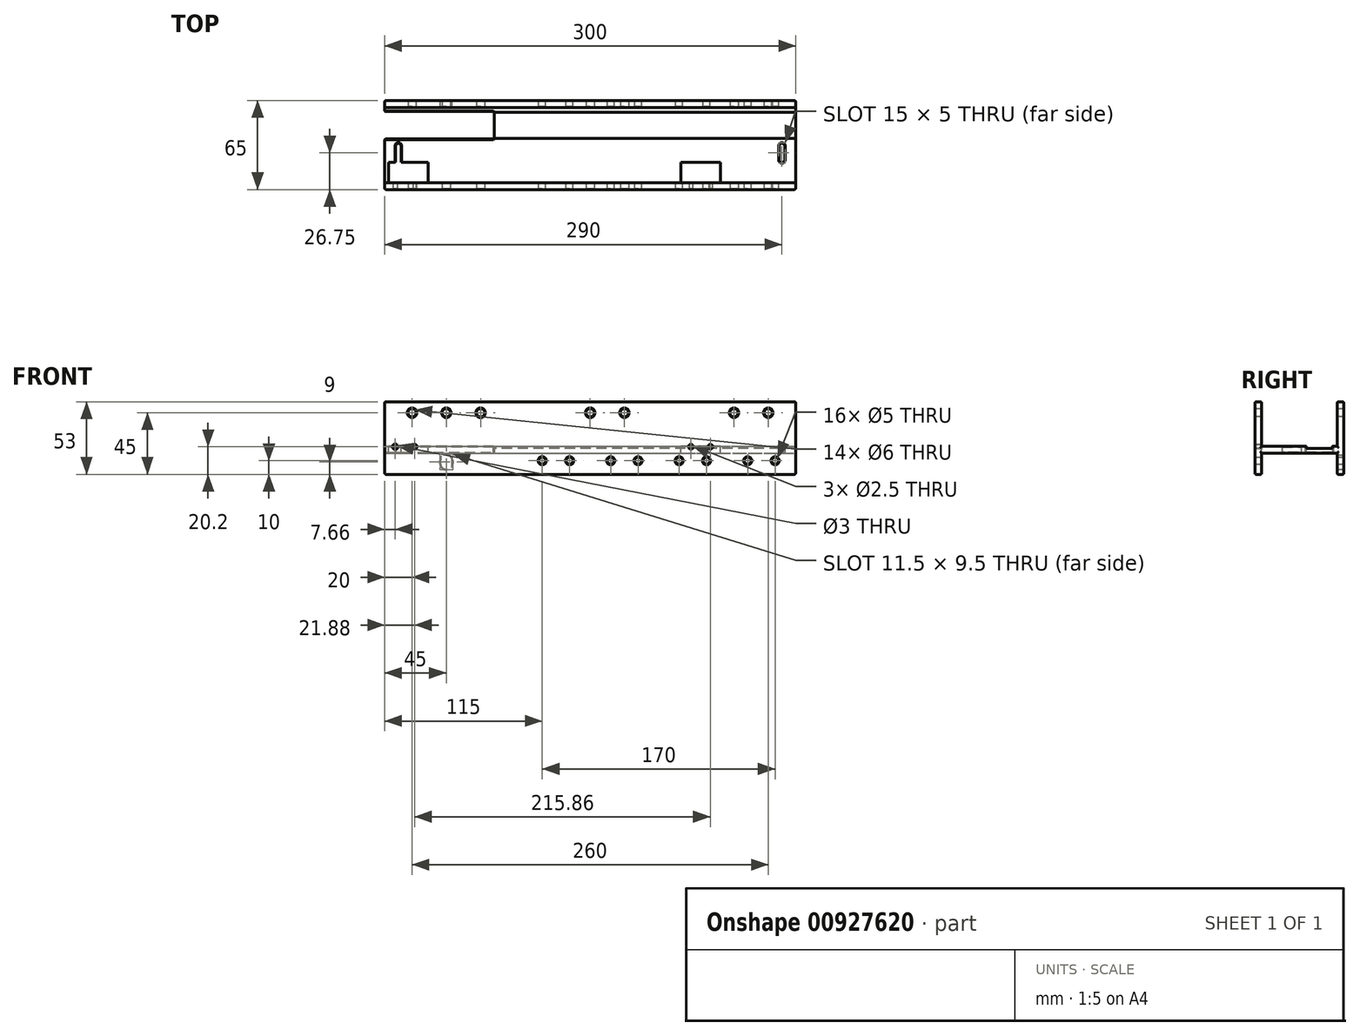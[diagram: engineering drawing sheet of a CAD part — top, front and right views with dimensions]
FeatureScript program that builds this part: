
annotation { "Feature Type Name" : "Feature", "Feature Type Description" : "" }
export const myFeature = defineFeature(function(context is Context, id is Id, definition is map)
    precondition{}
    {
        {
            var Q0;
            Q0=qCreatedBy(makeId("Right.planeOp"),FACE);
            var sketch = newSketch(context, id + "F0", { "sketchPlane" : qUnion([Q0])});
            skLineSegment(sketch, "E0", {"start": v(32.5, 30.09) * mm, "end": v(32.5, -3.64) * mm, "construction": true});
            skLineSegment(sketch, "E1", {"start": v(32.5, 20.5) * mm, "end": v(5, 20.5) * mm});
            skLineSegment(sketch, "E2", {"start": v(5, 20.5) * mm, "end": v(5, 53) * mm});
            skLineSegment(sketch, "E3", {"start": v(5, 53) * mm, "end": v(0, 53) * mm});
            skLineSegment(sketch, "E4", {"start": v(0, 53) * mm, "end": v(0, 0) * mm});
            skLineSegment(sketch, "E5", {"start": v(0, 0) * mm, "end": v(5, 0) * mm});
            skLineSegment(sketch, "E6", {"start": v(5, 0) * mm, "end": v(5, 15.5) * mm});
            skLineSegment(sketch, "E7", {"start": v(5, 15.5) * mm, "end": v(32.5, 15.5) * mm});
            skLineSegment(sketch, "E8.MirrorCS", {"start": v(32.5, 20.5) * mm, "end": v(60, 20.5) * mm});
            skLineSegment(sketch, "E9.MirrorCS", {"start": v(60, 15.5) * mm, "end": v(32.5, 15.5) * mm});
            skLineSegment(sketch, "E10.MirrorCS", {"start": v(60, 20.5) * mm, "end": v(60, 53) * mm});
            skLineSegment(sketch, "E11.MirrorCS", {"start": v(60, 53) * mm, "end": v(65, 53) * mm});
            skLineSegment(sketch, "E12.MirrorCS", {"start": v(65, 53) * mm, "end": v(65, 0) * mm});
            skLineSegment(sketch, "E13.MirrorCS", {"start": v(65, 0) * mm, "end": v(60, 0) * mm});
            skLineSegment(sketch, "E14.MirrorCS", {"start": v(60, 0) * mm, "end": v(60, 15.5) * mm});
            skLineSegment(sketch, "E15", {"start": v(26.34, 45) * mm, "end": v(97.95, 45) * mm, "construction": true});
            skLineSegment(sketch, "E16", {"start": v(29.5, 35.5) * mm, "end": v(100.2, 35.5) * mm, "construction": true});
            skLineSegment(sketch, "E17", {"start": v(30.7, 31) * mm, "end": v(101, 31) * mm, "construction": true});
            skSolve(sketch);
        }
        {
            var Q0;
            Q0=makeQuery(id+"F0.imprint","IMPRINT",FACE,{"disambiguationData":[TD([[makeQuery(id+"F0.imprint","IMPRINT",EDGE,{"derivedFrom":sQuery(id+"F0.wireOp",EDGE,"E1")}),1.0]])]});
            extrude(context, id + "F1", {"entities" : qUnion([Q0]), "oppositeDirection" : true, "depth" : 300 * mm, "offsetDistance" : 25 * mm});
        }
        {
            var Q0;
            Q0=makeQuery(id+"F1.opExtrude","SWEPT_FACE",FACE,{"disambiguationData":[OSD([sQuery(id+"F0.wireOp",EDGE,"E1"),sQuery(id+"F0.wireOp",EDGE,"E8.MirrorCS")])]});
            var sketch = newSketch(context, id + "F2", { "sketchPlane" : qUnion([Q0])});
            skLineSegment(sketch, "E18", {"start": v(-313.86, 45) * mm, "end": v(29.43, 45) * mm, "construction": true});
            skLineSegment(sketch, "E19", {"start": v(-150, 123.79) * mm, "end": v(-150, -54.38) * mm, "construction": true});
            skPoint(sketch, "E19.startSnap0", {"position": v(-150, 5) * mm});
            skLineSegment(sketch, "E20.MirrorCS", {"start": v(-220, 57) * mm, "end": v(-220, 45) * mm});
            skLineSegment(sketch, "E21.MirrorCS", {"start": v(-220, 37) * mm, "end": v(-220, 45) * mm});
            skLineSegment(sketch, "E22.MirrorCS", {"start": v(-300, 57) * mm, "end": v(-220, 57) * mm});
            skLineSegment(sketch, "E23.MirrorCS", {"start": v(-300, 37) * mm, "end": v(-220, 37) * mm});
            skSolve(sketch);
        }
        {
            var Q0;
            Q0=makeQuery(id+"F2.imprint","IMPRINT",FACE,{"disambiguationData":[TD([[makeQuery(id+"F2.imprint","IMPRINT",EDGE,{"derivedFrom":sQuery(id+"F2.wireOp",EDGE,"E20.MirrorCS")}),-1.0]])]});
            var Q1;
            {var subQ1=sQuery(id+"F2.wireOp",EDGE,"GCHkkF9p-yWQI-8tYB-lPff-ol5Ikm6K2We2");Q1=makeQuery(id+"F2.imprint","IMPRINT",FACE,{"disambiguationData":[TD([[makeQuery(id+"F2.imprint","IMPRINT",EDGE,{"derivedFrom":subQ1}),1.0]])]});}
            extrude(context, id + "F3", {"entities" : qUnion([Q0, Q1]), "operationType" : NewBodyOperationType.REMOVE, "endBound" : BoundingType.THROUGH_ALL, "oppositeDirection" : true, "depth" : 25 * mm, "offsetDistance" : 25 * mm});
        }
        {
            var Q0;
            Q0=makeQuery(id+"F1.opExtrude","SWEPT_EDGE",EDGE,{"disambiguationData":[OSD([sQuery(id+"F0.wireOp",EDGE,"E11.MirrorCS"),sQuery(id+"F0.wireOp",EDGE,"E12.MirrorCS")])]});
            var Q1;
            Q1=makeQuery(id+"F1.opExtrude","SWEPT_EDGE",EDGE,{"disambiguationData":[OSD([sQuery(id+"F0.wireOp",EDGE,"E3"),sQuery(id+"F0.wireOp",EDGE,"E4")])]});
            var Q2;
            Q2=makeQuery(id+"F1.opExtrude","SWEPT_EDGE",EDGE,{"disambiguationData":[OSD([sQuery(id+"F0.wireOp",EDGE,"E4"),sQuery(id+"F0.wireOp",EDGE,"E5")])]});
            var Q3;
            Q3=makeQuery(id+"F1.opExtrude","SWEPT_EDGE",EDGE,{"disambiguationData":[OSD([sQuery(id+"F0.wireOp",EDGE,"E5"),sQuery(id+"F0.wireOp",EDGE,"E6")])]});
            var Q4;
            Q4=makeQuery(id+"F1.opExtrude","SWEPT_EDGE",EDGE,{"disambiguationData":[OSD([sQuery(id+"F0.wireOp",EDGE,"E13.MirrorCS"),sQuery(id+"F0.wireOp",EDGE,"E14.MirrorCS")])]});
            var Q5;
            Q5=makeQuery(id+"F1.opExtrude","SWEPT_EDGE",EDGE,{"disambiguationData":[OSD([sQuery(id+"F0.wireOp",EDGE,"E12.MirrorCS"),sQuery(id+"F0.wireOp",EDGE,"E13.MirrorCS")])]});
            var Q6;
            Q6=makeQuery(id+"F1.opExtrude","SWEPT_EDGE",EDGE,{"disambiguationData":[OSD([sQuery(id+"F0.wireOp",EDGE,"E2"),sQuery(id+"F0.wireOp",EDGE,"E3")])]});
            var Q7;
            Q7=makeQuery(id+"F1.opExtrude","SWEPT_EDGE",EDGE,{"disambiguationData":[OSD([sQuery(id+"F0.wireOp",EDGE,"E10.MirrorCS"),sQuery(id+"F0.wireOp",EDGE,"E11.MirrorCS")])]});
            var Q8;
            Q8=makeQuery(id+"F1.opExtrude","CAP_EDGE",EDGE,{"disambiguationData":[OSD([sQuery(id+"F0.wireOp",EDGE,"E4")])],"isStart":true});
            var Q9;
            Q9=makeQuery(id+"F1.opExtrude","CAP_EDGE",EDGE,{"disambiguationData":[OSD([sQuery(id+"F0.wireOp",EDGE,"E2")])],"isStart":true});
            var Q10;
            {var subQ0=sQuery(id+"F0.wireOp",EDGE,"E8.MirrorCS");var subQ1=sQuery(id+"F0.wireOp",EDGE,"E2");var subQ2=sQuery(id+"F0.wireOp",EDGE,"E1");Q10=makeQuery(id+"F3.boolean.opBoolean","SPLIT",EDGE,{"disambiguationData":[TD([makeQuery(id+"F1.opExtrude","SWEPT_FACE",FACE,{"disambiguationData":[OSD([subQ1])]})])],"derivedFrom":makeQuery(id+"F1.opExtrude","CAP_EDGE",EDGE,{"disambiguationData":[OSD([subQ2,subQ0])],"isStart":true})});}
            var Q11;
            Q11=makeQuery(id+"F1.opExtrude","CAP_EDGE",EDGE,{"disambiguationData":[OSD([sQuery(id+"F0.wireOp",EDGE,"E6")])],"isStart":true});
            var Q12;
            Q12=makeQuery(id+"F1.opExtrude","CAP_EDGE",EDGE,{"disambiguationData":[OSD([sQuery(id+"F0.wireOp",EDGE,"E3")])],"isStart":true});
            var Q13;
            Q13=makeQuery(id+"F1.opExtrude","CAP_EDGE",EDGE,{"disambiguationData":[OSD([sQuery(id+"F0.wireOp",EDGE,"E5")])],"isStart":true});
            var Q14;
            Q14=makeQuery(id+"F1.opExtrude","CAP_EDGE",EDGE,{"disambiguationData":[OSD([sQuery(id+"F0.wireOp",EDGE,"E13.MirrorCS")])],"isStart":true});
            var Q15;
            Q15=makeQuery(id+"F1.opExtrude","CAP_EDGE",EDGE,{"disambiguationData":[OSD([sQuery(id+"F0.wireOp",EDGE,"E11.MirrorCS")])],"isStart":true});
            var Q16;
            Q16=makeQuery(id+"F1.opExtrude","CAP_EDGE",EDGE,{"disambiguationData":[OSD([sQuery(id+"F0.wireOp",EDGE,"E12.MirrorCS")])],"isStart":true});
            var Q17;
            Q17=makeQuery(id+"F1.opExtrude","CAP_EDGE",EDGE,{"disambiguationData":[OSD([sQuery(id+"F0.wireOp",EDGE,"E10.MirrorCS")])],"isStart":true});
            var Q18;
            Q18=makeQuery(id+"F1.opExtrude","CAP_EDGE",EDGE,{"disambiguationData":[OSD([sQuery(id+"F0.wireOp",EDGE,"E14.MirrorCS")])],"isStart":true});
            var Q19;
            {var subQ0=sQuery(id+"F0.wireOp",EDGE,"E10.MirrorCS");var subQ1=sQuery(id+"F0.wireOp",EDGE,"E8.MirrorCS");var subQ2=sQuery(id+"F0.wireOp",EDGE,"E1");Q19=makeQuery(id+"F3.boolean.opBoolean","SPLIT",EDGE,{"disambiguationData":[TD([makeQuery(id+"F1.opExtrude","SWEPT_FACE",FACE,{"disambiguationData":[OSD([subQ0])]})])],"derivedFrom":makeQuery(id+"F1.opExtrude","CAP_EDGE",EDGE,{"disambiguationData":[OSD([subQ2,subQ1])],"isStart":true})});}
            var Q20;
            {var subQ0=sQuery(id+"F0.wireOp",EDGE,"E9.MirrorCS");var subQ1=sQuery(id+"F0.wireOp",EDGE,"E7");var subQ2=sQuery(id+"F0.wireOp",EDGE,"E6");Q20=makeQuery(id+"F3.boolean.opBoolean","SPLIT",EDGE,{"disambiguationData":[TD([makeQuery(id+"F1.opExtrude","SWEPT_FACE",FACE,{"disambiguationData":[OSD([subQ2])]})])],"derivedFrom":makeQuery(id+"F1.opExtrude","CAP_EDGE",EDGE,{"disambiguationData":[OSD([subQ1,subQ0])],"isStart":true})});}
            var Q21;
            Q21=makeQuery(id+"F1.opExtrude","CAP_EDGE",EDGE,{"disambiguationData":[OSD([sQuery(id+"F0.wireOp",EDGE,"E5")])],"isStart":false});
            var Q22;
            Q22=makeQuery(id+"F1.opExtrude","CAP_EDGE",EDGE,{"disambiguationData":[OSD([sQuery(id+"F0.wireOp",EDGE,"E4")])],"isStart":false});
            var Q23;
            Q23=makeQuery(id+"F1.opExtrude","CAP_EDGE",EDGE,{"disambiguationData":[OSD([sQuery(id+"F0.wireOp",EDGE,"E3")])],"isStart":false});
            var Q24;
            Q24=makeQuery(id+"F1.opExtrude","CAP_EDGE",EDGE,{"disambiguationData":[OSD([sQuery(id+"F0.wireOp",EDGE,"E2")])],"isStart":false});
            var Q25;
            Q25=makeQuery(id+"F1.opExtrude","CAP_EDGE",EDGE,{"disambiguationData":[OSD([sQuery(id+"F0.wireOp",EDGE,"E6")])],"isStart":false});
            var Q26;
            {var subQ0=sQuery(id+"F0.wireOp",EDGE,"E9.MirrorCS");var subQ1=sQuery(id+"F0.wireOp",EDGE,"E7");var subQ2=sQuery(id+"F0.wireOp",EDGE,"E6");Q26=makeQuery(id+"F3.boolean.opBoolean","SPLIT",EDGE,{"disambiguationData":[TD([makeQuery(id+"F1.opExtrude","SWEPT_FACE",FACE,{"disambiguationData":[OSD([subQ2])]})])],"derivedFrom":makeQuery(id+"F1.opExtrude","CAP_EDGE",EDGE,{"disambiguationData":[OSD([subQ1,subQ0])],"isStart":false})});}
            var Q27;
            {var subQ0=sQuery(id+"F0.wireOp",EDGE,"E8.MirrorCS");var subQ1=sQuery(id+"F0.wireOp",EDGE,"E2");var subQ2=sQuery(id+"F0.wireOp",EDGE,"E1");Q27=makeQuery(id+"F3.boolean.opBoolean","SPLIT",EDGE,{"disambiguationData":[TD([makeQuery(id+"F1.opExtrude","SWEPT_FACE",FACE,{"disambiguationData":[OSD([subQ1])]})])],"derivedFrom":makeQuery(id+"F1.opExtrude","CAP_EDGE",EDGE,{"disambiguationData":[OSD([subQ2,subQ0])],"isStart":false})});}
            var Q28;
            Q28=makeQuery(id+"F1.opExtrude","CAP_EDGE",EDGE,{"disambiguationData":[OSD([sQuery(id+"F0.wireOp",EDGE,"E14.MirrorCS")])],"isStart":false});
            var Q29;
            Q29=makeQuery(id+"F1.opExtrude","CAP_EDGE",EDGE,{"disambiguationData":[OSD([sQuery(id+"F0.wireOp",EDGE,"E13.MirrorCS")])],"isStart":false});
            var Q30;
            Q30=makeQuery(id+"F1.opExtrude","CAP_EDGE",EDGE,{"disambiguationData":[OSD([sQuery(id+"F0.wireOp",EDGE,"E12.MirrorCS")])],"isStart":false});
            var Q31;
            Q31=makeQuery(id+"F1.opExtrude","CAP_EDGE",EDGE,{"disambiguationData":[OSD([sQuery(id+"F0.wireOp",EDGE,"E11.MirrorCS")])],"isStart":false});
            var Q32;
            Q32=makeQuery(id+"F1.opExtrude","CAP_EDGE",EDGE,{"disambiguationData":[OSD([sQuery(id+"F0.wireOp",EDGE,"E10.MirrorCS")])],"isStart":false});
            var Q33;
            {var subQ0=sQuery(id+"F0.wireOp",EDGE,"E10.MirrorCS");var subQ1=sQuery(id+"F0.wireOp",EDGE,"E8.MirrorCS");var subQ2=sQuery(id+"F0.wireOp",EDGE,"E1");Q33=makeQuery(id+"F3.boolean.opBoolean","SPLIT",EDGE,{"disambiguationData":[TD([makeQuery(id+"F1.opExtrude","SWEPT_FACE",FACE,{"disambiguationData":[OSD([subQ0])]})])],"derivedFrom":makeQuery(id+"F1.opExtrude","CAP_EDGE",EDGE,{"disambiguationData":[OSD([subQ2,subQ1])],"isStart":false})});}
            var Q34;
            {var subQ0=sQuery(id+"F0.wireOp",EDGE,"E14.MirrorCS");var subQ1=sQuery(id+"F0.wireOp",EDGE,"E9.MirrorCS");var subQ2=sQuery(id+"F0.wireOp",EDGE,"E7");Q34=makeQuery(id+"F3.boolean.opBoolean","SPLIT",EDGE,{"disambiguationData":[TD([makeQuery(id+"F1.opExtrude","SWEPT_FACE",FACE,{"disambiguationData":[OSD([subQ0])]})])],"derivedFrom":makeQuery(id+"F1.opExtrude","CAP_EDGE",EDGE,{"disambiguationData":[OSD([subQ2,subQ1])],"isStart":false})});}
            fillet(context, id + "F4", {"entities" : qUnion([Q0, Q1, Q2, Q3, Q4, Q5, Q6, Q7, Q8, Q9, Q10, Q11, Q12, Q13, Q14, Q15, Q16, Q17, Q18, Q19, Q20, Q21, Q22, Q23, Q24, Q25, Q26, Q27, Q28, Q29, Q30, Q31, Q32, Q33, Q34]), "radius" : 1 * mm, "tangentPropagation" : true, "allowEdgeOverflow" : false});
        }
        {
            var Q0;
            Q0=qCreatedBy(makeId("Front.planeOp"),FACE);
            var sketch = newSketch(context, id + "F5", { "sketchPlane" : qUnion([Q0])});
            skLineSegment(sketch, "E24.0.0", {"start": v(-299, 1) * mm, "end": v(-1, 1) * mm});
            skLineSegment(sketch, "E24.0.1", {"start": v(-1, 1) * mm, "end": v(-1, 52) * mm});
            skLineSegment(sketch, "E24.0.2", {"start": v(-1, 52) * mm, "end": v(-299, 52) * mm});
            skLineSegment(sketch, "E24.0.3", {"start": v(-299, 52) * mm, "end": v(-299, 1) * mm});
            skLineSegment(sketch, "E25", {"start": v(-345.84, 45) * mm, "end": v(41.43, 45) * mm, "construction": true});
            skCircle(sketch, "E26", {"center": v(-20, 45) * mm, "radius": 3 * mm});
            skCircle(sketch, "E27.1.0.0", {"center": v(-45, 45) * mm, "radius": 3 * mm});
            skLineSegment(sketch, "E27.direction1", {"start": v(-20, 45) * mm, "end": v(-45, 45) * mm, "construction": true});
            skCircle(sketch, "E28", {"center": v(-280, 45) * mm, "radius": 3 * mm});
            skCircle(sketch, "E29.1.0.0", {"center": v(-255, 45) * mm, "radius": 3 * mm});
            skCircle(sketch, "E29.2.0.0", {"center": v(-230, 45) * mm, "radius": 3 * mm});
            skLineSegment(sketch, "E29.direction1", {"start": v(-280, 45) * mm, "end": v(-255, 45) * mm, "construction": true});
            skLineSegment(sketch, "E30", {"start": v(-150, 104.95) * mm, "end": v(-150, -59.13) * mm, "construction": true});
            skCircle(sketch, "E31", {"center": v(-150, 45) * mm, "radius": 3 * mm});
            skCircle(sketch, "E32.1.0.0", {"center": v(-125, 45) * mm, "radius": 3 * mm});
            skLineSegment(sketch, "E32.direction1", {"start": v(-150, 45) * mm, "end": v(-125, 45) * mm, "construction": true});
            skLineSegment(sketch, "E33.direction1", {"start": v(-150, 45) * mm, "end": v(-175, 45) * mm, "construction": true});
            skCircle(sketch, "E34", {"center": v(-45, 45) * mm, "radius": 9.5 * mm, "construction": true});
            skLineSegment(sketch, "E35", {"start": v(-54.5, 62.62) * mm, "end": v(-54.5, 11.97) * mm, "construction": true});
            skLineSegment(sketch, "E36", {"start": v(-57.5, 61.94) * mm, "end": v(-57.5, 10.88) * mm, "construction": true});
            skLineSegment(sketch, "E37", {"start": v(-94.96, 20.2) * mm, "end": v(-48.41, 20.2) * mm, "construction": true});
            skLineSegment(sketch, "E38", {"start": v(-94.06, 14.9) * mm, "end": v(-44.37, 14.9) * mm, "construction": true});
            skCircle(sketch, "E39", {"center": v(-62.26, 20.2) * mm, "radius": 1.25 * mm});
            skCircle(sketch, "E40", {"center": v(-76.48, 20.2) * mm, "radius": 1.25 * mm});
            skCircle(sketch, "E41", {"center": v(-230, 45) * mm, "radius": 9.5 * mm, "construction": true});
            skLineSegment(sketch, "E42", {"start": v(-297.1, 57.68) * mm, "end": v(-297.1, 12.3) * mm, "construction": true});
            skLineSegment(sketch, "E43", {"start": v(-224.68, 20.2) * mm, "end": v(-186.08, 20.2) * mm, "construction": true});
            skCircle(sketch, "E44", {"center": v(-292.34, 20.2) * mm, "radius": 1.5 * mm});
            skCircle(sketch, "E45", {"center": v(-278.12, 20.2) * mm, "radius": 1.25 * mm});
            skLineSegment(sketch, "E46", {"start": v(-217.85, 25.5) * mm, "end": v(-182.53, 25.5) * mm, "construction": true});
            skLineSegment(sketch, "E47", {"start": v(-218.26, 14.9) * mm, "end": v(-182.12, 14.9) * mm, "construction": true});
            skLineSegment(sketch, "E48", {"start": v(-92.25, 25.5) * mm, "end": v(-56.75, 25.5) * mm, "construction": true});
            skLineSegment(sketch, "E49", {"start": v(-273.36, 59.39) * mm, "end": v(-273.36, 11.5) * mm, "construction": true});
            skLineSegment(sketch, "E50", {"start": v(-247.58, 30.5) * mm, "end": v(-217.06, 30.5) * mm, "construction": true});
            skLineSegment(sketch, "E51", {"start": v(-30.25, 30.5) * mm, "end": v(-63.73, 30.5) * mm, "construction": true});
            skLineSegment(sketch, "E52", {"start": v(-69.37, 53.38) * mm, "end": v(-69.37, 2.85) * mm, "construction": true});
            skLineSegment(sketch, "E53", {"start": v(-285.23, 36.68) * mm, "end": v(-285.23, 10.56) * mm, "construction": true});
            skLineSegment(sketch, "E54", {"start": v(-215.5, 60.74) * mm, "end": v(-215.5, -20.98) * mm, "construction": true});
            skSolve(sketch);
        }
        {
            var Q0;
            Q0=makeQuery(id+"F5.imprint","IMPRINT",FACE,{"disambiguationData":[TD([[makeQuery(id+"F5.imprint","IMPRINT",EDGE,{"derivedFrom":sQuery(id+"F5.wireOp",EDGE,"E26")}),1.0]])]});
            var Q1;
            Q1=makeQuery(id+"F5.imprint","IMPRINT",FACE,{"disambiguationData":[TD([[makeQuery(id+"F5.imprint","IMPRINT",EDGE,{"derivedFrom":sQuery(id+"F5.wireOp",EDGE,"E27.1.0.0")}),1.0]])]});
            var Q2;
            Q2=makeQuery(id+"F5.imprint","IMPRINT",FACE,{"disambiguationData":[TD([[makeQuery(id+"F5.imprint","IMPRINT",EDGE,{"derivedFrom":sQuery(id+"F5.wireOp",EDGE,"E27.2.0.0")}),1.0]])]});
            var Q3;
            Q3=makeQuery(id+"F5.imprint","IMPRINT",FACE,{"disambiguationData":[TD([[makeQuery(id+"F5.imprint","IMPRINT",EDGE,{"derivedFrom":sQuery(id+"F5.wireOp",EDGE,"E32.2.0.0")}),1.0]])]});
            var Q4;
            Q4=makeQuery(id+"F5.imprint","IMPRINT",FACE,{"disambiguationData":[TD([[makeQuery(id+"F5.imprint","IMPRINT",EDGE,{"derivedFrom":sQuery(id+"F5.wireOp",EDGE,"E32.1.0.0")}),1.0]])]});
            var Q5;
            Q5=makeQuery(id+"F5.imprint","IMPRINT",FACE,{"disambiguationData":[TD([[makeQuery(id+"F5.imprint","IMPRINT",EDGE,{"derivedFrom":sQuery(id+"F5.wireOp",EDGE,"E31")}),1.0]])]});
            var Q6;
            Q6=makeQuery(id+"F5.imprint","IMPRINT",FACE,{"disambiguationData":[TD([[makeQuery(id+"F5.imprint","IMPRINT",EDGE,{"derivedFrom":sQuery(id+"F5.wireOp",EDGE,"E33.1.0.0")}),1.0]])]});
            var Q7;
            Q7=makeQuery(id+"F5.imprint","IMPRINT",FACE,{"disambiguationData":[TD([[makeQuery(id+"F5.imprint","IMPRINT",EDGE,{"derivedFrom":sQuery(id+"F5.wireOp",EDGE,"E28")}),1.0]])]});
            var Q8;
            Q8=makeQuery(id+"F5.imprint","IMPRINT",FACE,{"disambiguationData":[TD([[makeQuery(id+"F5.imprint","IMPRINT",EDGE,{"derivedFrom":sQuery(id+"F5.wireOp",EDGE,"E29.1.0.0")}),1.0]])]});
            var Q9;
            Q9=makeQuery(id+"F5.imprint","IMPRINT",FACE,{"disambiguationData":[TD([[makeQuery(id+"F5.imprint","IMPRINT",EDGE,{"derivedFrom":sQuery(id+"F5.wireOp",EDGE,"E29.2.0.0")}),1.0]])]});
            var Q10;
            Q10=makeQuery(id+"F5.imprint","IMPRINT",FACE,{"disambiguationData":[TD([[makeQuery(id+"F5.imprint","IMPRINT",EDGE,{"derivedFrom":sQuery(id+"F5.wireOp",EDGE,"E33.2.0.0")}),1.0]])]});
            extrude(context, id + "F6", {"entities" : qUnion([Q0, Q1, Q2, Q3, Q4, Q5, Q6, Q7, Q8, Q9, Q10]), "operationType" : NewBodyOperationType.REMOVE, "endBound" : BoundingType.THROUGH_ALL, "oppositeDirection" : true, "depth" : 25 * mm, "offsetDistance" : 25 * mm});
        }
        {
            var Q0;
            Q0=makeQuery(id+"F6.boolean.opBoolean","COPY",FACE,{"disambiguationData":[TD([makeQuery(id+"F1.opExtrude","SWEPT_FACE",FACE,{"disambiguationData":[OSD([sQuery(id+"F0.wireOp",EDGE,"E2")])]})])],"derivedFrom":makeQuery(id+"F6.opExtrude","SWEPT_FACE",FACE,{"disambiguationData":[OSD([sQuery(id+"F5.wireOp",EDGE,"E26")])]})});
            var Q1;
            Q1=makeQuery(id+"F6.boolean.opBoolean","COPY",FACE,{"disambiguationData":[TD([makeQuery(id+"F1.opExtrude","SWEPT_FACE",FACE,{"disambiguationData":[OSD([sQuery(id+"F0.wireOp",EDGE,"E2")])]})])],"derivedFrom":makeQuery(id+"F6.opExtrude","SWEPT_FACE",FACE,{"disambiguationData":[OSD([sQuery(id+"F5.wireOp",EDGE,"E27.1.0.0")])]})});
            var Q2;
            Q2=makeQuery(id+"F6.boolean.opBoolean","COPY",FACE,{"disambiguationData":[TD([makeQuery(id+"F1.opExtrude","SWEPT_FACE",FACE,{"disambiguationData":[OSD([sQuery(id+"F0.wireOp",EDGE,"E2")])]})])],"derivedFrom":makeQuery(id+"F6.opExtrude","SWEPT_FACE",FACE,{"disambiguationData":[OSD([sQuery(id+"F5.wireOp",EDGE,"E27.2.0.0")])]})});
            var Q3;
            Q3=makeQuery(id+"F6.boolean.opBoolean","COPY",FACE,{"disambiguationData":[TD([makeQuery(id+"F1.opExtrude","SWEPT_FACE",FACE,{"disambiguationData":[OSD([sQuery(id+"F0.wireOp",EDGE,"E2")])]})])],"derivedFrom":makeQuery(id+"F6.opExtrude","SWEPT_FACE",FACE,{"disambiguationData":[OSD([sQuery(id+"F5.wireOp",EDGE,"E32.2.0.0")])]})});
            var Q4;
            Q4=makeQuery(id+"F6.boolean.opBoolean","COPY",FACE,{"disambiguationData":[TD([makeQuery(id+"F1.opExtrude","SWEPT_FACE",FACE,{"disambiguationData":[OSD([sQuery(id+"F0.wireOp",EDGE,"E2")])]})])],"derivedFrom":makeQuery(id+"F6.opExtrude","SWEPT_FACE",FACE,{"disambiguationData":[OSD([sQuery(id+"F5.wireOp",EDGE,"E32.1.0.0")])]})});
            var Q5;
            Q5=makeQuery(id+"F6.boolean.opBoolean","COPY",FACE,{"disambiguationData":[TD([makeQuery(id+"F1.opExtrude","SWEPT_FACE",FACE,{"disambiguationData":[OSD([sQuery(id+"F0.wireOp",EDGE,"E2")])]})])],"derivedFrom":makeQuery(id+"F6.opExtrude","SWEPT_FACE",FACE,{"disambiguationData":[OSD([sQuery(id+"F5.wireOp",EDGE,"E31")])]})});
            var Q6;
            Q6=makeQuery(id+"F6.boolean.opBoolean","COPY",FACE,{"disambiguationData":[TD([makeQuery(id+"F1.opExtrude","SWEPT_FACE",FACE,{"disambiguationData":[OSD([sQuery(id+"F0.wireOp",EDGE,"E2")])]})])],"derivedFrom":makeQuery(id+"F6.opExtrude","SWEPT_FACE",FACE,{"disambiguationData":[OSD([sQuery(id+"F5.wireOp",EDGE,"E33.1.0.0")])]})});
            var Q7;
            Q7=makeQuery(id+"F6.boolean.opBoolean","COPY",FACE,{"disambiguationData":[TD([makeQuery(id+"F1.opExtrude","SWEPT_FACE",FACE,{"disambiguationData":[OSD([sQuery(id+"F0.wireOp",EDGE,"E2")])]})])],"derivedFrom":makeQuery(id+"F6.opExtrude","SWEPT_FACE",FACE,{"disambiguationData":[OSD([sQuery(id+"F5.wireOp",EDGE,"E33.2.0.0")])]})});
            var Q8;
            Q8=makeQuery(id+"F6.boolean.opBoolean","COPY",FACE,{"disambiguationData":[TD([makeQuery(id+"F1.opExtrude","SWEPT_FACE",FACE,{"disambiguationData":[OSD([sQuery(id+"F0.wireOp",EDGE,"E2")])]})])],"derivedFrom":makeQuery(id+"F6.opExtrude","SWEPT_FACE",FACE,{"disambiguationData":[OSD([sQuery(id+"F5.wireOp",EDGE,"E29.2.0.0")])]})});
            var Q9;
            Q9=makeQuery(id+"F6.boolean.opBoolean","COPY",FACE,{"disambiguationData":[TD([makeQuery(id+"F1.opExtrude","SWEPT_FACE",FACE,{"disambiguationData":[OSD([sQuery(id+"F0.wireOp",EDGE,"E2")])]})])],"derivedFrom":makeQuery(id+"F6.opExtrude","SWEPT_FACE",FACE,{"disambiguationData":[OSD([sQuery(id+"F5.wireOp",EDGE,"E29.1.0.0")])]})});
            var Q10;
            Q10=makeQuery(id+"F6.boolean.opBoolean","COPY",FACE,{"disambiguationData":[TD([makeQuery(id+"F1.opExtrude","SWEPT_FACE",FACE,{"disambiguationData":[OSD([sQuery(id+"F0.wireOp",EDGE,"E2")])]})])],"derivedFrom":makeQuery(id+"F6.opExtrude","SWEPT_FACE",FACE,{"disambiguationData":[OSD([sQuery(id+"F5.wireOp",EDGE,"E28")])]})});
            var Q11;
            Q11=makeQuery(id+"F6.boolean.opBoolean","COPY",FACE,{"disambiguationData":[TD([makeQuery(id+"F1.opExtrude","SWEPT_FACE",FACE,{"disambiguationData":[OSD([sQuery(id+"F0.wireOp",EDGE,"E10.MirrorCS")])]})])],"derivedFrom":makeQuery(id+"F6.opExtrude","SWEPT_FACE",FACE,{"disambiguationData":[OSD([sQuery(id+"F5.wireOp",EDGE,"E26")])]})});
            var Q12;
            Q12=makeQuery(id+"F6.boolean.opBoolean","COPY",FACE,{"disambiguationData":[TD([makeQuery(id+"F1.opExtrude","SWEPT_FACE",FACE,{"disambiguationData":[OSD([sQuery(id+"F0.wireOp",EDGE,"E10.MirrorCS")])]})])],"derivedFrom":makeQuery(id+"F6.opExtrude","SWEPT_FACE",FACE,{"disambiguationData":[OSD([sQuery(id+"F5.wireOp",EDGE,"E27.1.0.0")])]})});
            var Q13;
            Q13=makeQuery(id+"F6.boolean.opBoolean","COPY",FACE,{"disambiguationData":[TD([makeQuery(id+"F1.opExtrude","SWEPT_FACE",FACE,{"disambiguationData":[OSD([sQuery(id+"F0.wireOp",EDGE,"E10.MirrorCS")])]})])],"derivedFrom":makeQuery(id+"F6.opExtrude","SWEPT_FACE",FACE,{"disambiguationData":[OSD([sQuery(id+"F5.wireOp",EDGE,"E27.2.0.0")])]})});
            var Q14;
            Q14=makeQuery(id+"F6.boolean.opBoolean","COPY",FACE,{"disambiguationData":[TD([makeQuery(id+"F1.opExtrude","SWEPT_FACE",FACE,{"disambiguationData":[OSD([sQuery(id+"F0.wireOp",EDGE,"E10.MirrorCS")])]})])],"derivedFrom":makeQuery(id+"F6.opExtrude","SWEPT_FACE",FACE,{"disambiguationData":[OSD([sQuery(id+"F5.wireOp",EDGE,"E32.2.0.0")])]})});
            var Q15;
            Q15=makeQuery(id+"F6.boolean.opBoolean","COPY",FACE,{"disambiguationData":[TD([makeQuery(id+"F1.opExtrude","SWEPT_FACE",FACE,{"disambiguationData":[OSD([sQuery(id+"F0.wireOp",EDGE,"E10.MirrorCS")])]})])],"derivedFrom":makeQuery(id+"F6.opExtrude","SWEPT_FACE",FACE,{"disambiguationData":[OSD([sQuery(id+"F5.wireOp",EDGE,"E32.1.0.0")])]})});
            var Q16;
            Q16=makeQuery(id+"F6.boolean.opBoolean","COPY",FACE,{"disambiguationData":[TD([makeQuery(id+"F1.opExtrude","SWEPT_FACE",FACE,{"disambiguationData":[OSD([sQuery(id+"F0.wireOp",EDGE,"E10.MirrorCS")])]})])],"derivedFrom":makeQuery(id+"F6.opExtrude","SWEPT_FACE",FACE,{"disambiguationData":[OSD([sQuery(id+"F5.wireOp",EDGE,"E31")])]})});
            var Q17;
            Q17=makeQuery(id+"F6.boolean.opBoolean","COPY",FACE,{"disambiguationData":[TD([makeQuery(id+"F1.opExtrude","SWEPT_FACE",FACE,{"disambiguationData":[OSD([sQuery(id+"F0.wireOp",EDGE,"E10.MirrorCS")])]})])],"derivedFrom":makeQuery(id+"F6.opExtrude","SWEPT_FACE",FACE,{"disambiguationData":[OSD([sQuery(id+"F5.wireOp",EDGE,"E33.1.0.0")])]})});
            var Q18;
            Q18=makeQuery(id+"F6.boolean.opBoolean","COPY",FACE,{"disambiguationData":[TD([makeQuery(id+"F1.opExtrude","SWEPT_FACE",FACE,{"disambiguationData":[OSD([sQuery(id+"F0.wireOp",EDGE,"E10.MirrorCS")])]})])],"derivedFrom":makeQuery(id+"F6.opExtrude","SWEPT_FACE",FACE,{"disambiguationData":[OSD([sQuery(id+"F5.wireOp",EDGE,"E33.2.0.0")])]})});
            var Q19;
            Q19=makeQuery(id+"F6.boolean.opBoolean","COPY",FACE,{"disambiguationData":[TD([makeQuery(id+"F1.opExtrude","SWEPT_FACE",FACE,{"disambiguationData":[OSD([sQuery(id+"F0.wireOp",EDGE,"E10.MirrorCS")])]})])],"derivedFrom":makeQuery(id+"F6.opExtrude","SWEPT_FACE",FACE,{"disambiguationData":[OSD([sQuery(id+"F5.wireOp",EDGE,"E29.2.0.0")])]})});
            var Q20;
            Q20=makeQuery(id+"F6.boolean.opBoolean","COPY",FACE,{"disambiguationData":[TD([makeQuery(id+"F1.opExtrude","SWEPT_FACE",FACE,{"disambiguationData":[OSD([sQuery(id+"F0.wireOp",EDGE,"E10.MirrorCS")])]})])],"derivedFrom":makeQuery(id+"F6.opExtrude","SWEPT_FACE",FACE,{"disambiguationData":[OSD([sQuery(id+"F5.wireOp",EDGE,"E29.1.0.0")])]})});
            var Q21;
            Q21=makeQuery(id+"F6.boolean.opBoolean","COPY",FACE,{"disambiguationData":[TD([makeQuery(id+"F1.opExtrude","SWEPT_FACE",FACE,{"disambiguationData":[OSD([sQuery(id+"F0.wireOp",EDGE,"E10.MirrorCS")])]})])],"derivedFrom":makeQuery(id+"F6.opExtrude","SWEPT_FACE",FACE,{"disambiguationData":[OSD([sQuery(id+"F5.wireOp",EDGE,"E28")])]})});
            chamfer(context, id + "F7", {"entities" : qUnion([Q0, Q1, Q2, Q3, Q4, Q5, Q6, Q7, Q8, Q9, Q10, Q11, Q12, Q13, Q14, Q15, Q16, Q17, Q18, Q19, Q20, Q21]), "width" : 0.5 * mm, "tangentPropagation" : true});
        }
        {
            var Q0;
            Q0=qCreatedBy(makeId("Top.planeOp"),FACE);
            var sketch = newSketch(context, id + "F8", { "sketchPlane" : qUnion([Q0])});
            skLineSegment(sketch, "E55", {"start": v(-327.25, 26.75) * mm, "end": v(48.68, 26.75) * mm, "construction": true});
            skLineSegment(sketch, "E56", {"start": v(-150, 101.3) * mm, "end": v(-150, -68.09) * mm, "construction": true});
            skLineSegment(sketch, "E57", {"start": v(-10, 12.13) * mm, "end": v(-10, 41.3) * mm, "construction": true});
            skLineSegment(sketch, "E58", {"start": v(-12, 21.75) * mm, "end": v(-12, 31.75) * mm});
            skLineSegment(sketch, "E59.MirrorCS", {"start": v(-8, 21.75) * mm, "end": v(-8, 31.75) * mm});
            skArc(sketch, "E60", {"start": v(-12, 21.75) * mm, "mid": v(-10, 19.75) * mm, "end": v(-8, 21.75) * mm});
            skArc(sketch, "E61.MirrorCS", {"start": v(-12, 31.75) * mm, "mid": v(-10, 33.75) * mm, "end": v(-8, 31.75) * mm});
            skLineSegment(sketch, "E62.MirrorCS", {"start": v(-292, 26.75) * mm, "end": v(-292, 31.75) * mm});
            skLineSegment(sketch, "E63.MirrorCS", {"start": v(-288, 26.75) * mm, "end": v(-288, 31.75) * mm});
            skArc(sketch, "E64.MirrorCS", {"start": v(-288, 31.75) * mm, "mid": v(-290, 33.75) * mm, "end": v(-292, 31.75) * mm});
            skPoint(sketch, "E65.orphan", {"position": v(-288, 21.75) * mm});
            skPoint(sketch, "E66.orphan", {"position": v(-292, 21.75) * mm});
            skLineSegment(sketch, "E67", {"start": v(-288, 26.75) * mm, "end": v(-288, 14.75) * mm});
            skLineSegment(sketch, "E68", {"start": v(-288, 14.75) * mm, "end": v(-292, 14.75) * mm});
            skLineSegment(sketch, "E69", {"start": v(-292, 14.75) * mm, "end": v(-292, 26.75) * mm});
            skSolve(sketch);
        }
        {
            var Q0;
            Q0 = qSketchRegion(id + "F8", true);
            extrude(context, id + "F9", {"entities" : qUnion([Q0]), "operationType" : NewBodyOperationType.REMOVE, "depth" : 25 * mm, "offsetDistance" : 25 * mm});
        }
        {
            var Q0;
            Q0=makeQuery(id+"F1.opExtrude","SWEPT_FACE",FACE,{"disambiguationData":[OSD([sQuery(id+"F0.wireOp",EDGE,"E12.MirrorCS")])]});
            var sketch = newSketch(context, id + "F10", { "sketchPlane" : qUnion([Q0])});
            skLineSegment(sketch, "E70", {"start": v(-12, 10) * mm, "end": v(316.82, 10) * mm, "construction": true});
            skCircle(sketch, "E71", {"center": v(15, 10) * mm, "radius": 2.5 * mm});
            skCircle(sketch, "E72", {"center": v(35, 10) * mm, "radius": 2.5 * mm});
            skCircle(sketch, "E73", {"center": v(185, 10) * mm, "radius": 2.5 * mm});
            skCircle(sketch, "E74", {"center": v(165, 10) * mm, "radius": 2.5 * mm});
            skCircle(sketch, "E75", {"center": v(65, 10) * mm, "radius": 2.5 * mm});
            skCircle(sketch, "E76", {"center": v(85, 10) * mm, "radius": 2.5 * mm});
            skCircle(sketch, "E77", {"center": v(135, 10) * mm, "radius": 2.5 * mm});
            skCircle(sketch, "E78", {"center": v(115, 10) * mm, "radius": 2.5 * mm});
            skLineSegment(sketch, "E79", {"start": v(262.83, 10) * mm, "end": v(304.88, 10) * mm, "construction": true});
            skLineSegment(sketch, "E80", {"start": v(259.25, 10) * mm, "end": v(259.25, 8) * mm});
            skLineSegment(sketch, "E81", {"start": v(250.75, 10) * mm, "end": v(250.75, 8) * mm});
            skLineSegment(sketch, "E82", {"start": v(255, 20.42) * mm, "end": v(255, -6.23) * mm, "construction": true});
            skArc(sketch, "E83", {"start": v(259.25, 10) * mm, "mid": v(255, 14.25) * mm, "end": v(250.75, 10) * mm});
            skArc(sketch, "E84", {"start": v(250.75, 8) * mm, "mid": v(255, 3.75) * mm, "end": v(259.25, 8) * mm});
            skSolve(sketch);
        }
        {
            var Q0;
            Q0=makeQuery(id+"F10.imprint","IMPRINT",FACE,{"disambiguationData":[TD([[makeQuery(id+"F10.imprint","IMPRINT",EDGE,{"derivedFrom":sQuery(id+"F10.wireOp",EDGE,"E71")}),1.0]])]});
            var Q1;
            Q1=makeQuery(id+"F10.imprint","IMPRINT",FACE,{"disambiguationData":[TD([[makeQuery(id+"F10.imprint","IMPRINT",EDGE,{"derivedFrom":sQuery(id+"F10.wireOp",EDGE,"E72")}),1.0]])]});
            var Q2;
            Q2=makeQuery(id+"F10.imprint","IMPRINT",FACE,{"disambiguationData":[TD([[makeQuery(id+"F10.imprint","IMPRINT",EDGE,{"derivedFrom":sQuery(id+"F10.wireOp",EDGE,"E75")}),1.0]])]});
            var Q3;
            Q3=makeQuery(id+"F10.imprint","IMPRINT",FACE,{"disambiguationData":[TD([[makeQuery(id+"F10.imprint","IMPRINT",EDGE,{"derivedFrom":sQuery(id+"F10.wireOp",EDGE,"E76")}),1.0]])]});
            var Q4;
            Q4=makeQuery(id+"F10.imprint","IMPRINT",FACE,{"disambiguationData":[TD([[makeQuery(id+"F10.imprint","IMPRINT",EDGE,{"derivedFrom":sQuery(id+"F10.wireOp",EDGE,"E78")}),1.0]])]});
            var Q5;
            Q5=makeQuery(id+"F10.imprint","IMPRINT",FACE,{"disambiguationData":[TD([[makeQuery(id+"F10.imprint","IMPRINT",EDGE,{"derivedFrom":sQuery(id+"F10.wireOp",EDGE,"E77")}),1.0]])]});
            var Q6;
            Q6=makeQuery(id+"F10.imprint","IMPRINT",FACE,{"disambiguationData":[TD([[makeQuery(id+"F10.imprint","IMPRINT",EDGE,{"derivedFrom":sQuery(id+"F10.wireOp",EDGE,"E74")}),1.0]])]});
            var Q7;
            Q7=makeQuery(id+"F10.imprint","IMPRINT",FACE,{"disambiguationData":[TD([[makeQuery(id+"F10.imprint","IMPRINT",EDGE,{"derivedFrom":sQuery(id+"F10.wireOp",EDGE,"E73")}),1.0]])]});
            extrude(context, id + "F11", {"entities" : qUnion([Q0, Q1, Q2, Q3, Q4, Q5, Q6, Q7]), "operationType" : NewBodyOperationType.REMOVE, "endBound" : BoundingType.THROUGH_ALL, "oppositeDirection" : true, "depth" : 25 * mm, "offsetDistance" : 25 * mm});
        }
        {
            var Q0;
            Q0=makeQuery(id+"F11.boolean.opBoolean","COPY",FACE,{"disambiguationData":[TD([makeQuery(id+"F1.opExtrude","SWEPT_FACE",FACE,{"disambiguationData":[OSD([sQuery(id+"F0.wireOp",EDGE,"E4")])]})])],"derivedFrom":makeQuery(id+"F11.opExtrude","SWEPT_FACE",FACE,{"disambiguationData":[OSD([sQuery(id+"F10.wireOp",EDGE,"E73")])]})});
            var Q1;
            Q1=makeQuery(id+"F11.boolean.opBoolean","COPY",FACE,{"disambiguationData":[TD([makeQuery(id+"F1.opExtrude","SWEPT_FACE",FACE,{"disambiguationData":[OSD([sQuery(id+"F0.wireOp",EDGE,"E4")])]})])],"derivedFrom":makeQuery(id+"F11.opExtrude","SWEPT_FACE",FACE,{"disambiguationData":[OSD([sQuery(id+"F10.wireOp",EDGE,"E74")])]})});
            var Q2;
            Q2=makeQuery(id+"F11.boolean.opBoolean","COPY",FACE,{"disambiguationData":[TD([makeQuery(id+"F1.opExtrude","SWEPT_FACE",FACE,{"disambiguationData":[OSD([sQuery(id+"F0.wireOp",EDGE,"E12.MirrorCS")])]})])],"derivedFrom":makeQuery(id+"F11.opExtrude","SWEPT_FACE",FACE,{"disambiguationData":[OSD([sQuery(id+"F10.wireOp",EDGE,"E73")])]})});
            var Q3;
            Q3=makeQuery(id+"F11.boolean.opBoolean","COPY",FACE,{"disambiguationData":[TD([makeQuery(id+"F1.opExtrude","SWEPT_FACE",FACE,{"disambiguationData":[OSD([sQuery(id+"F0.wireOp",EDGE,"E12.MirrorCS")])]})])],"derivedFrom":makeQuery(id+"F11.opExtrude","SWEPT_FACE",FACE,{"disambiguationData":[OSD([sQuery(id+"F10.wireOp",EDGE,"E74")])]})});
            var Q4;
            Q4=makeQuery(id+"F11.boolean.opBoolean","COPY",FACE,{"disambiguationData":[TD([makeQuery(id+"F1.opExtrude","SWEPT_FACE",FACE,{"disambiguationData":[OSD([sQuery(id+"F0.wireOp",EDGE,"E12.MirrorCS")])]})])],"derivedFrom":makeQuery(id+"F11.opExtrude","SWEPT_FACE",FACE,{"disambiguationData":[OSD([sQuery(id+"F10.wireOp",EDGE,"E72")])]})});
            var Q5;
            Q5=makeQuery(id+"F11.boolean.opBoolean","COPY",FACE,{"disambiguationData":[TD([makeQuery(id+"F1.opExtrude","SWEPT_FACE",FACE,{"disambiguationData":[OSD([sQuery(id+"F0.wireOp",EDGE,"E12.MirrorCS")])]})])],"derivedFrom":makeQuery(id+"F11.opExtrude","SWEPT_FACE",FACE,{"disambiguationData":[OSD([sQuery(id+"F10.wireOp",EDGE,"E71")])]})});
            var Q6;
            Q6=makeQuery(id+"F11.boolean.opBoolean","COPY",FACE,{"disambiguationData":[TD([makeQuery(id+"F1.opExtrude","SWEPT_FACE",FACE,{"disambiguationData":[OSD([sQuery(id+"F0.wireOp",EDGE,"E4")])]})])],"derivedFrom":makeQuery(id+"F11.opExtrude","SWEPT_FACE",FACE,{"disambiguationData":[OSD([sQuery(id+"F10.wireOp",EDGE,"E72")])]})});
            var Q7;
            Q7=makeQuery(id+"F11.boolean.opBoolean","COPY",FACE,{"disambiguationData":[TD([makeQuery(id+"F1.opExtrude","SWEPT_FACE",FACE,{"disambiguationData":[OSD([sQuery(id+"F0.wireOp",EDGE,"E4")])]})])],"derivedFrom":makeQuery(id+"F11.opExtrude","SWEPT_FACE",FACE,{"disambiguationData":[OSD([sQuery(id+"F10.wireOp",EDGE,"E71")])]})});
            chamfer(context, id + "F12", {"entities" : qUnion([Q0, Q1, Q2, Q3, Q4, Q5, Q6, Q7]), "width" : 0.5 * mm, "tangentPropagation" : true});
        }
        {
            var Q0;
            Q0=makeQuery(id+"F11.boolean.opBoolean","COPY",FACE,{"disambiguationData":[TD([makeQuery(id+"F1.opExtrude","SWEPT_FACE",FACE,{"disambiguationData":[OSD([sQuery(id+"F0.wireOp",EDGE,"E12.MirrorCS")])]})])],"derivedFrom":makeQuery(id+"F11.opExtrude","SWEPT_FACE",FACE,{"disambiguationData":[OSD([sQuery(id+"F10.wireOp",EDGE,"E75")])]})});
            var Q1;
            Q1=makeQuery(id+"F11.boolean.opBoolean","COPY",FACE,{"disambiguationData":[TD([makeQuery(id+"F1.opExtrude","SWEPT_FACE",FACE,{"disambiguationData":[OSD([sQuery(id+"F0.wireOp",EDGE,"E12.MirrorCS")])]})])],"derivedFrom":makeQuery(id+"F11.opExtrude","SWEPT_FACE",FACE,{"disambiguationData":[OSD([sQuery(id+"F10.wireOp",EDGE,"E76")])]})});
            var Q2;
            Q2=makeQuery(id+"F11.boolean.opBoolean","COPY",FACE,{"disambiguationData":[TD([makeQuery(id+"F1.opExtrude","SWEPT_FACE",FACE,{"disambiguationData":[OSD([sQuery(id+"F0.wireOp",EDGE,"E4")])]})])],"derivedFrom":makeQuery(id+"F11.opExtrude","SWEPT_FACE",FACE,{"disambiguationData":[OSD([sQuery(id+"F10.wireOp",EDGE,"E75")])]})});
            var Q3;
            Q3=makeQuery(id+"F11.boolean.opBoolean","COPY",FACE,{"disambiguationData":[TD([makeQuery(id+"F1.opExtrude","SWEPT_FACE",FACE,{"disambiguationData":[OSD([sQuery(id+"F0.wireOp",EDGE,"E4")])]})])],"derivedFrom":makeQuery(id+"F11.opExtrude","SWEPT_FACE",FACE,{"disambiguationData":[OSD([sQuery(id+"F10.wireOp",EDGE,"E76")])]})});
            var Q4;
            Q4=makeQuery(id+"F11.boolean.opBoolean","COPY",FACE,{"disambiguationData":[TD([makeQuery(id+"F1.opExtrude","SWEPT_FACE",FACE,{"disambiguationData":[OSD([sQuery(id+"F0.wireOp",EDGE,"E12.MirrorCS")])]})])],"derivedFrom":makeQuery(id+"F11.opExtrude","SWEPT_FACE",FACE,{"disambiguationData":[OSD([sQuery(id+"F10.wireOp",EDGE,"E77")])]})});
            var Q5;
            Q5=makeQuery(id+"F11.boolean.opBoolean","COPY",FACE,{"disambiguationData":[TD([makeQuery(id+"F1.opExtrude","SWEPT_FACE",FACE,{"disambiguationData":[OSD([sQuery(id+"F0.wireOp",EDGE,"E12.MirrorCS")])]})])],"derivedFrom":makeQuery(id+"F11.opExtrude","SWEPT_FACE",FACE,{"disambiguationData":[OSD([sQuery(id+"F10.wireOp",EDGE,"E78")])]})});
            var Q6;
            Q6=makeQuery(id+"F11.boolean.opBoolean","COPY",FACE,{"disambiguationData":[TD([makeQuery(id+"F1.opExtrude","SWEPT_FACE",FACE,{"disambiguationData":[OSD([sQuery(id+"F0.wireOp",EDGE,"E4")])]})])],"derivedFrom":makeQuery(id+"F11.opExtrude","SWEPT_FACE",FACE,{"disambiguationData":[OSD([sQuery(id+"F10.wireOp",EDGE,"E78")])]})});
            var Q7;
            Q7=makeQuery(id+"F11.boolean.opBoolean","COPY",FACE,{"disambiguationData":[TD([makeQuery(id+"F1.opExtrude","SWEPT_FACE",FACE,{"disambiguationData":[OSD([sQuery(id+"F0.wireOp",EDGE,"E4")])]})])],"derivedFrom":makeQuery(id+"F11.opExtrude","SWEPT_FACE",FACE,{"disambiguationData":[OSD([sQuery(id+"F10.wireOp",EDGE,"E77")])]})});
            chamfer(context, id + "F13", {"entities" : qUnion([Q0, Q1, Q2, Q3, Q4, Q5, Q6, Q7]), "width" : 0.5 * mm, "tangentPropagation" : true});
        }
        {
            var Q0;
            Q0=makeQuery(id+"F9.boolean.opBoolean","COPY",FACE,{"derivedFrom":makeQuery(id+"F9.opExtrude","SWEPT_FACE",FACE,{"disambiguationData":[OSD([sQuery(id+"F8.wireOp",EDGE,"E58")])]})});
            var Q1;
            Q1=makeQuery(id+"F9.boolean.opBoolean","COPY",FACE,{"derivedFrom":makeQuery(id+"F9.opExtrude","SWEPT_FACE",FACE,{"disambiguationData":[OSD([sQuery(id+"F8.wireOp",EDGE,"E60")])]})});
            var Q2;
            Q2=makeQuery(id+"F9.boolean.opBoolean","INTERSECT",EDGE,{"derivedFrom":[makeQuery(id+"F1.opExtrude","SWEPT_FACE",FACE,{"disambiguationData":[OSD([sQuery(id+"F0.wireOp",EDGE,"E7"),sQuery(id+"F0.wireOp",EDGE,"E9.MirrorCS")])]}),makeQuery(id+"F9.opExtrude","SWEPT_FACE",FACE,{"disambiguationData":[OSD([sQuery(id+"F8.wireOp",EDGE,"E62.MirrorCS")])]})]});
            var Q3;
            Q3=makeQuery(id+"F9.boolean.opBoolean","INTERSECT",EDGE,{"derivedFrom":[makeQuery(id+"F1.opExtrude","SWEPT_FACE",FACE,{"disambiguationData":[OSD([sQuery(id+"F0.wireOp",EDGE,"E1"),sQuery(id+"F0.wireOp",EDGE,"E8.MirrorCS")])]}),makeQuery(id+"F9.opExtrude","SWEPT_FACE",FACE,{"disambiguationData":[OSD([sQuery(id+"F8.wireOp",EDGE,"E63.MirrorCS")])]})]});
            chamfer(context, id + "F14", {"entities" : qUnion([Q0, Q1, Q2, Q3]), "width" : 0.5 * mm, "tangentPropagation" : true});
        }
        {
            var Q0;
            Q0=makeQuery(id+"F10.imprint","IMPRINT",FACE,{"disambiguationData":[TD([[makeQuery(id+"F10.imprint","IMPRINT",EDGE,{"derivedFrom":sQuery(id+"F10.wireOp",EDGE,"E80")}),-1.0]])]});
            extrude(context, id + "F15", {"entities" : qUnion([Q0]), "operationType" : NewBodyOperationType.REMOVE, "oppositeDirection" : true, "depth" : 25 * mm, "offsetDistance" : 25 * mm});
        }
        {
            var Q0;
            Q0=makeQuery(id+"F15.boolean.opBoolean","COPY",FACE,{"derivedFrom":makeQuery(id+"F15.opExtrude","SWEPT_FACE",FACE,{"disambiguationData":[OSD([sQuery(id+"F10.wireOp",EDGE,"E83")])]})});
            var Q1;
            Q1=makeQuery(id+"F15.boolean.opBoolean","COPY",FACE,{"derivedFrom":makeQuery(id+"F15.opExtrude","SWEPT_FACE",FACE,{"disambiguationData":[OSD([sQuery(id+"F10.wireOp",EDGE,"E84")])]})});
            chamfer(context, id + "F16", {"entities" : qUnion([Q0, Q1]), "width" : 0.5 * mm, "tangentPropagation" : true});
        }
        {
            var Q0;
            Q0=makeQuery(id+"F3.boolean.opBoolean","COPY",FACE,{"derivedFrom":makeQuery(id+"F3.opExtrude","SWEPT_FACE",FACE,{"disambiguationData":[OSD([sQuery(id+"F2.wireOp",EDGE,"E20.MirrorCS"),sQuery(id+"F2.wireOp",EDGE,"E21.MirrorCS")])]})});
            chamfer(context, id + "F17", {"entities" : qUnion([Q0]), "width" : 0.5 * mm, "tangentPropagation" : true});
        }
        {
            var Q0;
            Q0=makeQuery(id+"F3.boolean.opBoolean","COPY",FACE,{"derivedFrom":makeQuery(id+"F3.opExtrude","SWEPT_FACE",FACE,{"disambiguationData":[OSD([sQuery(id+"F2.wireOp",EDGE,"E20.MirrorCS"),sQuery(id+"F2.wireOp",EDGE,"E21.MirrorCS")])]})});
            var sketch = newSketch(context, id + "F18", { "sketchPlane" : qUnion([Q0])});
            skLineSegment(sketch, "E85.bottom", {"start": v(-56.5, 22) * mm, "end": v(-37.5, 22) * mm});
            skLineSegment(sketch, "E85.top", {"start": v(-56.5, 19) * mm, "end": v(-37.5, 19) * mm});
            skLineSegment(sketch, "E85.left", {"start": v(-56.5, 22) * mm, "end": v(-56.5, 19) * mm});
            skLineSegment(sketch, "E85.right", {"start": v(-37.5, 22) * mm, "end": v(-37.5, 19) * mm});
            skSolve(sketch);
        }
        {
            var Q0;
            Q0 = qSketchRegion(id + "F18", true);
            extrude(context, id + "F19", {"entities" : qUnion([Q0]), "operationType" : NewBodyOperationType.REMOVE, "endBound" : BoundingType.THROUGH_ALL, "oppositeDirection" : true, "depth" : 25 * mm, "offsetDistance" : 25 * mm});
        }
        {
            var Q0;
            Q0=makeQuery(id+"F5.imprint","IMPRINT",FACE,{"disambiguationData":[TD([[makeQuery(id+"F5.imprint","IMPRINT",EDGE,{"derivedFrom":sQuery(id+"F5.wireOp",EDGE,"E40")}),1.0]])]});
            var Q1;
            Q1=makeQuery(id+"F5.imprint","IMPRINT",FACE,{"disambiguationData":[TD([[makeQuery(id+"F5.imprint","IMPRINT",EDGE,{"derivedFrom":sQuery(id+"F5.wireOp",EDGE,"E39")}),1.0]])]});
            var Q2;
            Q2=makeQuery(id+"F5.imprint","IMPRINT",FACE,{"disambiguationData":[TD([[makeQuery(id+"F5.imprint","IMPRINT",EDGE,{"derivedFrom":sQuery(id+"F5.wireOp",EDGE,"E44")}),1.0]])]});
            var Q3;
            Q3=makeQuery(id+"F5.imprint","IMPRINT",FACE,{"disambiguationData":[TD([[makeQuery(id+"F5.imprint","IMPRINT",EDGE,{"derivedFrom":sQuery(id+"F5.wireOp",EDGE,"E45")}),1.0]])]});
            extrude(context, id + "F20", {"entities" : qUnion([Q0, Q1, Q2, Q3]), "operationType" : NewBodyOperationType.REMOVE, "oppositeDirection" : true, "depth" : 6 * mm, "offsetDistance" : 25 * mm});
        }
        {
            var Q0;
            {var subQ0=sQuery(id+"F0.wireOp",EDGE,"E8.MirrorCS");var subQ1=sQuery(id+"F0.wireOp",EDGE,"E1");var subQ2=sQuery(id+"F0.wireOp",EDGE,"E2");var subQ3=makeQuery(id+"F1.opExtrude","SWEPT_FACE",FACE,{"disambiguationData":[OSD([subQ1,subQ0])]});var subQ6=makeQuery(id+"F1.opExtrude","SWEPT_FACE",FACE,{"disambiguationData":[OSD([subQ2])]});Q0=makeQuery(id+"F19.boolean.opBoolean","SPLIT",FACE,{"disambiguationData":[TD([subQ6])],"derivedFrom":subQ3});}
            var sketch = newSketch(context, id + "F21", { "sketchPlane" : qUnion([Q0])});
            skLineSegment(sketch, "E86", {"start": v(-297.1, 61.1) * mm, "end": v(-297.1, -2.97) * mm, "construction": true});
            skLineSegment(sketch, "E87.bottom", {"start": v(-297.1, 20) * mm, "end": v(-268.36, 20) * mm});
            skLineSegment(sketch, "E87.top", {"start": v(-297.1, 5) * mm, "end": v(-268.36, 5) * mm});
            skLineSegment(sketch, "E87.left", {"start": v(-297.1, 20) * mm, "end": v(-297.1, 5) * mm});
            skLineSegment(sketch, "E87.right", {"start": v(-268.36, 20) * mm, "end": v(-268.36, 5) * mm});
            skLineSegment(sketch, "E88", {"start": v(-55, 73.7) * mm, "end": v(-55, -31.52) * mm, "construction": true});
            skLineSegment(sketch, "E89.bottom", {"start": v(-55, 5) * mm, "end": v(-83.74, 5) * mm});
            skLineSegment(sketch, "E89.top", {"start": v(-55, 20) * mm, "end": v(-83.74, 20) * mm});
            skLineSegment(sketch, "E89.left", {"start": v(-55, 5) * mm, "end": v(-55, 20) * mm});
            skLineSegment(sketch, "E89.right", {"start": v(-83.74, 5) * mm, "end": v(-83.74, 20) * mm});
            skSolve(sketch);
        }
        {
            var Q0;
            Q0 = qSketchRegion(id + "F21", true);
            extrude(context, id + "F22", {"entities" : qUnion([Q0]), "operationType" : NewBodyOperationType.REMOVE, "endBound" : BoundingType.THROUGH_ALL, "oppositeDirection" : true, "depth" : 25 * mm, "offsetDistance" : 25 * mm});
        }
        {
            var Q0;
            Q0=makeQuery(id+"F20.boolean.opBoolean","COPY",FACE,{"derivedFrom":makeQuery(id+"F20.opExtrude","SWEPT_FACE",FACE,{"disambiguationData":[OSD([sQuery(id+"F5.wireOp",EDGE,"E40")])]})});
            var Q1;
            Q1=makeQuery(id+"F20.boolean.opBoolean","COPY",FACE,{"derivedFrom":makeQuery(id+"F20.opExtrude","SWEPT_FACE",FACE,{"disambiguationData":[OSD([sQuery(id+"F5.wireOp",EDGE,"E39")])]})});
            var Q2;
            Q2=makeQuery(id+"F20.boolean.opBoolean","COPY",FACE,{"derivedFrom":makeQuery(id+"F20.opExtrude","SWEPT_FACE",FACE,{"disambiguationData":[OSD([sQuery(id+"F5.wireOp",EDGE,"E44")])]})});
            var Q3;
            Q3=makeQuery(id+"F20.boolean.opBoolean","COPY",FACE,{"derivedFrom":makeQuery(id+"F20.opExtrude","SWEPT_FACE",FACE,{"disambiguationData":[OSD([sQuery(id+"F5.wireOp",EDGE,"E45")])]})});
            chamfer(context, id + "F23", {"entities" : qUnion([Q0, Q1, Q2, Q3]), "width" : 0.5 * mm, "tangentPropagation" : true});
        }
    });
